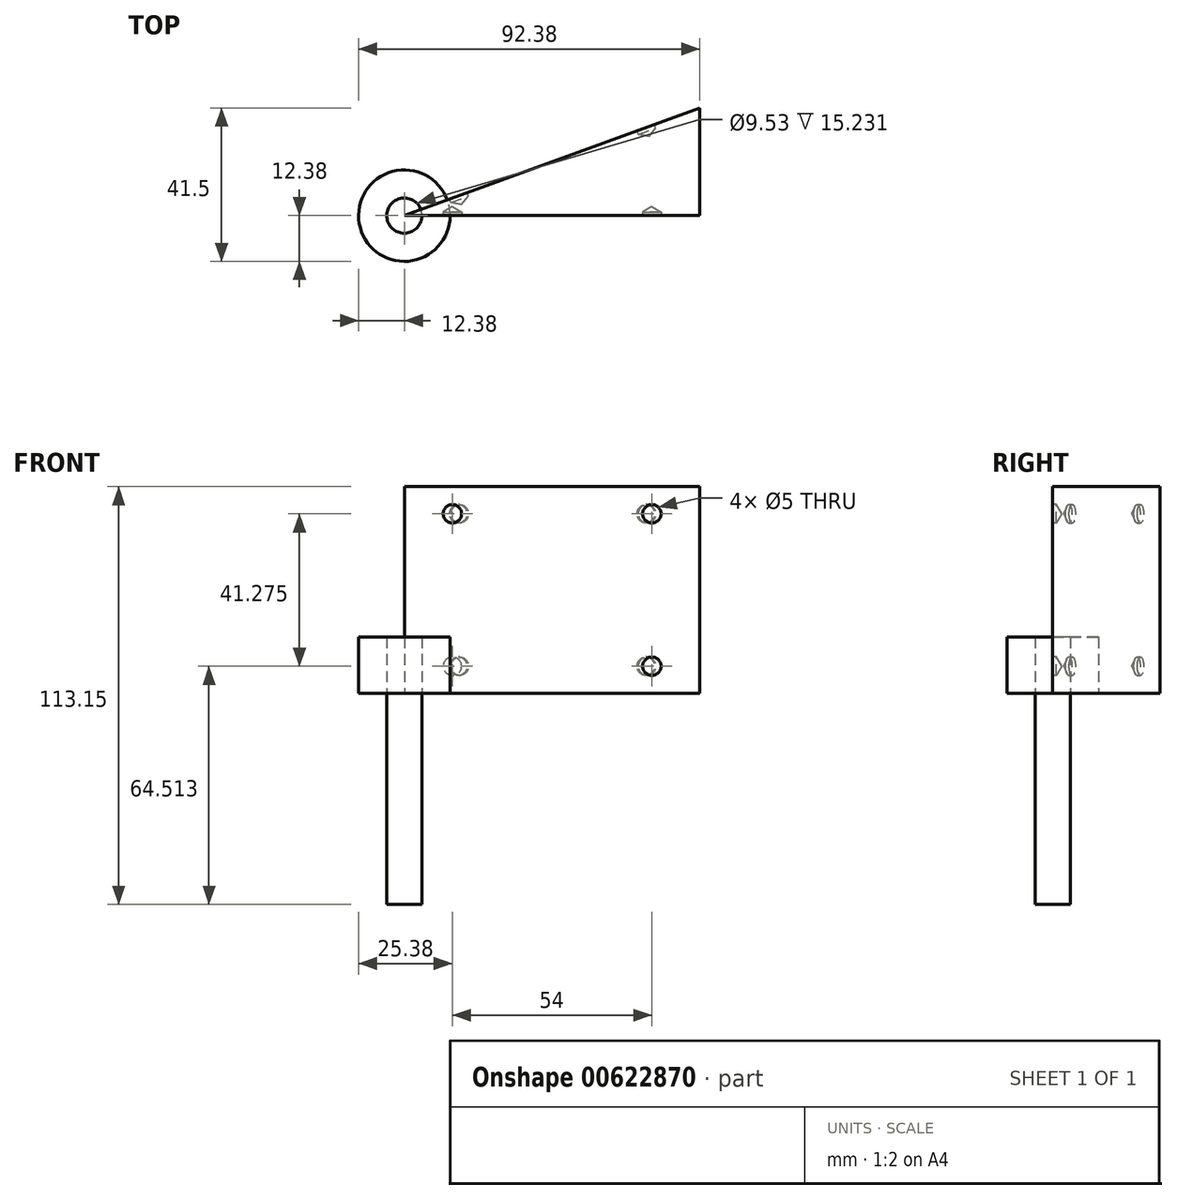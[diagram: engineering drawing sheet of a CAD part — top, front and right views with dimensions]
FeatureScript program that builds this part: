
annotation { "Feature Type Name" : "Feature", "Feature Type Description" : "" }
export const myFeature = defineFeature(function(context is Context, id is Id, definition is map)
    precondition{}
    {
        {
            var Q0;
            Q0=qCreatedBy(makeId("Top.planeOp"),FACE);
            var sketch = newSketch(context, id + "F0", { "sketchPlane" : qUnion([Q0])});
            skCircle(sketch, "E0", {"center": v(0, 0) * mm, "radius": 12.38 * mm});
            skCircle(sketch, "E1", {"center": v(0, 0) * mm, "radius": 4.76 * mm});
            skSolve(sketch);
        }
        {
            var Q0;
            Q0=makeQuery(id+"F0.imprint","IMPRINT",FACE,{"disambiguationData":[TD([[makeQuery(id+"F0.imprint","IMPRINT",EDGE,{"derivedFrom":sQuery(id+"F0.wireOp",EDGE,"E0")}),1.0]])]});
            extrude(context, id + "F1", {"entities" : qUnion([Q0]), "depth" : 15.24 * mm, "offsetDistance" : 25 * mm});
        }
        {
            var Q0;
            Q0=qCreatedBy(makeId("Top.planeOp"),FACE);
            var sketch = newSketch(context, id + "F2", { "sketchPlane" : qUnion([Q0])});
            skCircle(sketch, "E2.cCircle", {"center": v(0, 0) * mm, "radius": 8.25 * mm, "construction": true});
            skLineSegment(sketch, "E2.0", {"start": v(6.23, -5.41) * mm, "end": v(-1.57, -8.1) * mm});
            skLineSegment(sketch, "E2.1", {"start": v(-1.57, -8.1) * mm, "end": v(-7.8, -2.7) * mm});
            skLineSegment(sketch, "E2.2", {"start": v(-7.8, -2.7) * mm, "end": v(-6.23, 5.41) * mm});
            skLineSegment(sketch, "E2.3", {"start": v(-6.23, 5.41) * mm, "end": v(1.57, 8.1) * mm});
            skLineSegment(sketch, "E2.4", {"start": v(1.57, 8.1) * mm, "end": v(7.8, 2.7) * mm});
            skLineSegment(sketch, "E2.5", {"start": v(7.8, 2.7) * mm, "end": v(6.23, -5.41) * mm});
            skCircle(sketch, "E3", {"center": v(0, 0) * mm, "radius": 4.76 * mm});
            skSolve(sketch);
        }
        {
            var Q0;
            Q0=makeQuery(id+"F2.imprint","IMPRINT",FACE,{"disambiguationData":[TD([[makeQuery(id+"F2.imprint","IMPRINT",EDGE,{"derivedFrom":sQuery(id+"F2.wireOp",EDGE,"E2.0")}),-1.0]])]});
            var Q1;
            Q1=makeQuery(id+"F2.imprint","IMPRINT",FACE,{"disambiguationData":[TD([[makeQuery(id+"F2.imprint","IMPRINT",EDGE,{"derivedFrom":sQuery(id+"F2.wireOp",EDGE,"E3")}),1.0]])]});
            extrude(context, id + "F3", {"entities" : qUnion([Q0, Q1]), "depth" : 15 / 1625.6 * mm, "offsetDistance" : 25 * mm});
        }
        {
            var Q0;
            Q0=makeQuery(id+"F2.imprint","IMPRINT",FACE,{"disambiguationData":[TD([[makeQuery(id+"F2.imprint","IMPRINT",EDGE,{"derivedFrom":sQuery(id+"F2.wireOp",EDGE,"E3")}),1.0]])]});
            extrude(context, id + "F4", {"entities" : qUnion([Q0]), "operationType" : NewBodyOperationType.ADD, "oppositeDirection" : true, "depth" : 57.15 * mm, "offsetDistance" : 25 * mm});
        }
        {
            var Q0;
            Q0=qCreatedBy(makeId("Top.planeOp"),FACE);
            var sketch = newSketch(context, id + "F5", { "sketchPlane" : qUnion([Q0])});
            skLineSegment(sketch, "E4", {"start": v(0, 0) * mm, "end": v(80, 0) * mm});
            skLineSegment(sketch, "E5", {"start": v(80, 0) * mm, "end": v(80, 29.12) * mm});
            skLineSegment(sketch, "E6", {"start": v(80, 29.12) * mm, "end": v(0, 0) * mm});
            skSolve(sketch);
        }
        {
            var Q0;
            Q0=makeQuery(id+"F5.imprint","IMPRINT",FACE,{"disambiguationData":[TD([[makeQuery(id+"F5.imprint","IMPRINT",EDGE,{"derivedFrom":sQuery(id+"F5.wireOp",EDGE,"E4")}),1.0]])]});
            extrude(context, id + "F6", {"entities" : qUnion([Q0]), "depth" : 56 * mm, "offsetDistance" : 25 * mm});
        }
        {
            var Q0;
            Q0=makeQuery(id+"F6.opExtrude","SWEPT_FACE",FACE,{"disambiguationData":[OSD([sQuery(id+"F5.wireOp",EDGE,"E6")])]});
            var sketch = newSketch(context, id + "F7", { "sketchPlane" : qUnion([Q0])});
            skPoint(sketch, "E7", {"position": v(-69.57, 7.36) * mm});
            skPoint(sketch, "E8", {"position": v(-69.57, 48.64) * mm});
            skPoint(sketch, "E9", {"position": v(-15.57, 7.36) * mm});
            skPoint(sketch, "E10", {"position": v(-15.57, 48.64) * mm});
            skSolve(sketch);
        }
        {
            var Q0;
            Q0=makeQuery(id+"F6.opExtrude","SWEPT_FACE",FACE,{"disambiguationData":[OSD([sQuery(id+"F5.wireOp",EDGE,"E4")])]});
            var sketch = newSketch(context, id + "F8", { "sketchPlane" : qUnion([Q0])});
            skPoint(sketch, "E11", {"position": v(67, 48.64) * mm});
            skPoint(sketch, "E12", {"position": v(67, 7.36) * mm});
            skPoint(sketch, "E13", {"position": v(13, 7.36) * mm});
            skPoint(sketch, "E14", {"position": v(13, 48.64) * mm});
            skSolve(sketch);
        }
        {
            var Q0;
            Q0=sQuery(id+"F7.wireOp",VERTEX,"E10");
            var Q1;
            Q1=sQuery(id+"F7.wireOp",VERTEX,"E9");
            var Q2;
            Q2=sQuery(id+"F7.wireOp",VERTEX,"E7");
            var Q3;
            Q3=sQuery(id+"F7.wireOp",VERTEX,"E8");
            var Q4;
            Q4=sQuery(id+"F8.wireOp",VERTEX,"E14");
            var Q5;
            Q5=sQuery(id+"F8.wireOp",VERTEX,"E13");
            var Q6;
            Q6=sQuery(id+"F8.wireOp",VERTEX,"E11");
            var Q7;
            Q7=sQuery(id+"F8.wireOp",VERTEX,"E12");
            var Q8;
            Q8=makeQuery(id+"F6.opExtrude","SWEPT_BODY",BODY,{"disambiguationData":[OSD([sQuery(id+"F5.wireOp",EDGE,"E4"),sQuery(id+"F5.wireOp",EDGE,"E5"),sQuery(id+"F5.wireOp",EDGE,"E6")])]});
            hole(context, id + "F9", {"style" : HoleStyle.SIMPLE, "endStyle" : HoleEndStyle.BLIND, "standardTappedOrClearance" : lookupTablePath({ "standard" : "ISO", "size" : "5", "type" : "Drilled" }), "standardBlindInLast" : lookupTablePath({ "standard" : "ISO", "size" : "5", "type" : "Drilled" }), "holeDiameter" : 5 * mm, "majorDiameter" : 5 * mm, "holeDepth" : 1 * mm, "isTappedThrough" : true, "tappedDepth" : 12 * mm, "tapClearance" : 3, "locations" : qUnion([Q0, Q1, Q2, Q3, Q4, Q5, Q6, Q7]), "scope" : qUnion([Q8])});
        }
    });
